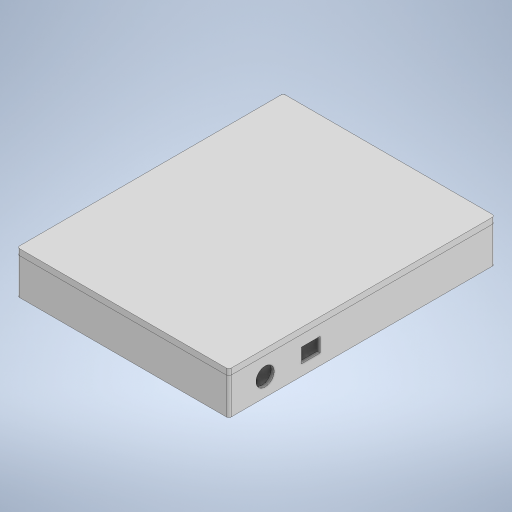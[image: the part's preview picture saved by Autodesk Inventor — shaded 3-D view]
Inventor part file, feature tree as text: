
AUTODESK INVENTOR PART (.ipt)
format: ipt  version: 2023 (Build 270158000, 158)  size: 258,560 bytes
history: native  units: mm
features: extrude x3, sketch x3, fillet x1, shell x1, projected_geometry x1
ambient origin geometry x8: Origin, YZ Plane, XZ Plane, XY Plane, X Axis, Y Axis, Z Axis, Center Point
bodies: Solid1 (feature_tree), Solid2 (feature_tree)
feature tree (9):
  extrude  "Extrusion1"  Depth=220.0mm
  extrude  "Extrusion2"  Depth=5.0mm
  fillet  "Fillet1"  Radius=5.0mm
  extrude  "Extrusion3"  Depth=2.0mm
  shell  "Shell1"  Thickness=15.0mm
  sketch  "Sketch1"  dims[d0=175.0mm d1=220.0mm]
  sketch  "Sketch2"  dims[d2=87.5mm d3=110.0mm d4=5.0mm d5=0.0mm]
  projected_geometry  "Projected Loop1"
  sketch  "Sketch3"  dims[d6=30.0mm d7=0.0mm d8=2.0mm d9=15.0mm d10=30.0mm d11=15.0mm d12=30.0mm d13=15.5mm d14=12.0mm d15=9.0mm d16=30.0mm d17=2.5mm d18=0.0mm d19=1.0mm d20=0.872665mm]
